# Revit family: IS_i-lifeS_E2109_BIM_GB
name_source: partatom
category: Plumbing Fixtures
units: mm (PartAtom-declared; Revit-internal decimal feet)

## family parameters
Always vertical = No
Cut with Voids When Loaded = No
OmniClass Number = 23.45.05.14.14
OmniClass Title = Sinks/Lavatories
Part Type = Normal
Room Calculation Point = No
Round Connector Dimension = Use Diameter
Shared = No
Work Plane-Based = No

## types (1)
- E210901 - i.life S 37cm Vessel Washbasin - White
    Accessories = https://www.idealstandard.co.uk
    AreaUnits = Millimetres
    BIMObjectName = IS_IdealStandard_Wall-HungHandRinseBasins_i.life_E2109
    BIMobject category = Wash Basins
    BIMobject category code = wash-basins
    BIMobject main category = Sanitary
    BIMobject main category code = sanitary
    BarCode = 5017830543916
    Brand = Ideal Standard
    Brand url = https://www.idealstandard.co.uk
    Category = Sanitary
    Classification = Basin
    Color = White
    ConnectionType = plumbing
    CurrencyUnit = £
    CurrentRevision = 1
    Date of publishing = 14/11/2022
    Description = i.life S 37cm vessel basin, 1 taphole , no overflow
    DurationUnit = years
    Edition number = 1
    ElementType = Fixed
    ExpectedLife = 99
    Features = 37cm vessel basin, 1 taphole , no overflow
    Finish = White
    GTIN code = https://5017830543916
    Help = https://www.idealstandard.co.uk
    IFC Classification = Sanitary Terminal
    IfcExportAs = IfcSanitaryTerminalType
    IfcExportType = WASHHANDBASIN
    Installation instructions = https://www.idealstandard.co.uk
    InstallationInstructions = https://www.idealstandard.co.uk
    LinearUnits = Millimetres
    MainColor = White
    MaintenanceInformation = https://www.idealstandard.co.uk
    Manufacturer = Ideal Standard
    Manufacturer name = Ideal standard test account
    ManufacturerURL = https://www.idealstandard.co.uk
    Material = Ceramics
    Material main = Ceramics
    Model = E210901
    ModelNumber = E210901
    ModelReference = E210901 - i.life S 37cm Vessel Washbasin - White
    NBS Reference Code = 45-35-70/369
    NBS Reference Description = Wall hung wash basins
    Name = Wall-HungHandRinseBasins_i.life_E2109_IdealStandard
    NettWeight = 6.2
    NominalDepth = 210 mm
    NominalHeight = 120 mm
    NominalLength = 210 mm
    NominalWidth = 370 mm
    OmniClass Code = 23-39 29 13 21 19
    OmniClass Description = Surface Water Retencion Basins
    PredefinedType = Sanitary
    Product Guid = 854d4f07-95af-4f5e-aa18-78e112e4a9ad
    Product SKU = E2109
    Product certification = https://www.idealstandard.co.uk
    Product data url = https://www.idealstandard.co.uk
    Product family = i.life
    Product group = Plumbing Fixtures
    Product name = TEMPO/EUROVIT H/R BSN 37X21 WHT NOF BXD
    Product url = https://www.idealstandard.co.uk
    ProductInformation = https://www.idealstandard.co.uk
    Shape = Sculpture
    Size = 370 x 210 x 120 mm
    Space = Internal
    SpareParts = https://www.idealstandard.co.uk
    Technical description = https://www.idealstandard.co.uk
    UNSPSC Code = 301815
    URL = https://www.idealstandard.co.uk
    Uniclass 1.4 Code = L7212
    Uniclass 1.4 Description = Washbasin
    Uniclass 2.0 Code = Pr_40_30_79_95
    Uniclass 2.0 Description = Wall-Hung Hand Rinse Basins
    Uniclass 2015 Code = Pr_40_20_96_96
    Uniclass 2015 Name = Wall-hung washbasins
    Uniclass2015Code = Pr_40_20_96_96
    Uniclass2015Title = Wall-hung washbasins
    Uniclass2015Version = v1.27
    Uniformat II Code = D2010
    Uniformat II Description = Plumbing Fixtures
    Version = 1
    VolumeUnits = litres
    WRASURL = https://www.wrasapprovals.co.uk
    WarrantyDescription = manufacturer warranty
    WarrantyDurationUnit = years
    Weight Net (Kg) = 6.2
    Youtube clip = https://www.youtube.com

## geometry (parser evidence)
native form markers: Sweep x1
no freeform markers — native parametric forms only
